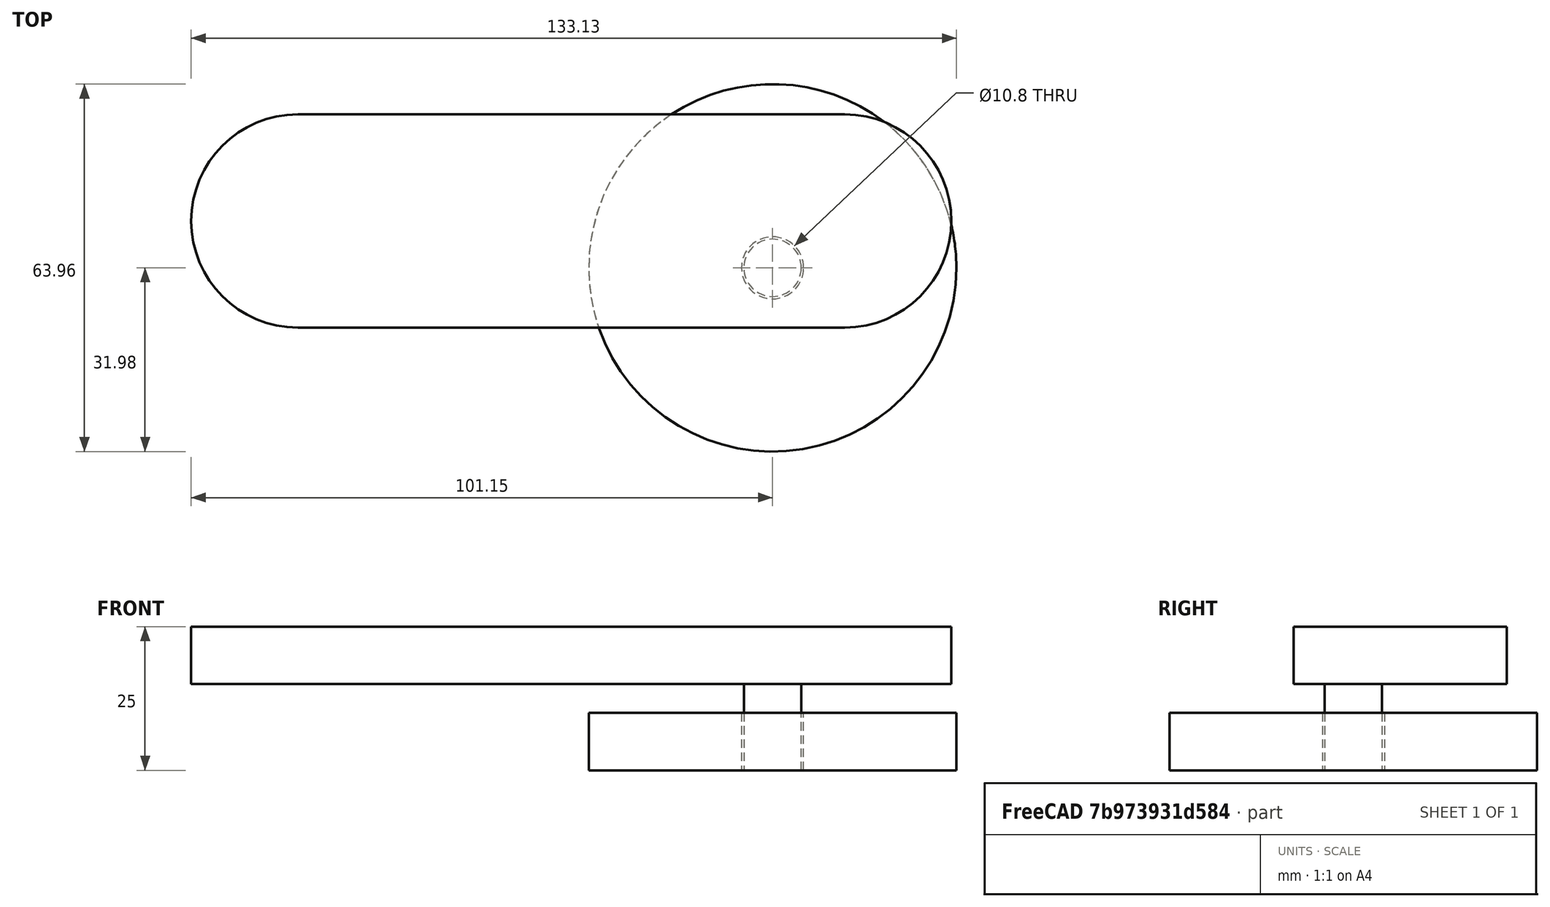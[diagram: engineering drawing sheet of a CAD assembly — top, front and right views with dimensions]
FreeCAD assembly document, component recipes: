
FREECAD ASSEMBLY — COMPONENT RECIPES ("assembly")

This assembly document has 3 components, labeled P0..P2 below (a component is one placed body or linked part). 3 of them carry a construction recipe — the FreeCAD feature program that regenerates the part from scratch, quoted from this document or its linked companion documents; the rest are supplied as boundary geometry only. No exploded tour is included for this assembly.
COMPONENT P0 — recipe-attached ("Cuerpo003", modeled in this document).
Construction recipe (the document's own serialized feature program — sketch geometry with constraints, then the solid features built on it; lengths are millimeters unless a unit is written):

FEATURE [Sketcher::SketchObject] Sketch
  ArcFitTolerance = 1e-06
  AttachmentSupport = -> [XY_Plane]
  FullyConstrained = false
  MakeInternals = false
  MapMode = 5
  sketch-geometry (2):
    g0: Circle CenterX=0 CenterY=0 CenterZ=0 NormalX=0 NormalY=0 NormalZ=1 AngleXU=0 Radius=31.9841
    g1: Circle CenterX=0 CenterY=0 CenterZ=0 NormalX=0 NormalY=0 NormalZ=1 AngleXU=0 Radius=5.40099
  constraints (2):
    c: Coincident(g0,g-1)
    c: Coincident(g1,g0)
FEATURE [PartDesign::Pad] Pad
  Direction = (0,0,1)
  Length = 10
  Length2 = 10
  Profile = -> Sketch
  ReferenceAxis = -> Sketch [N_Axis]
  Refine = true
  Suppressed = false
  Type = 0
FEATURE [PartDesign::Body] Body  label="Cuerpo"
  AllowCompound = false
  Group = -> [Sketch,Pad]
  Origin = -> Origin
  Tip = -> Pad
COMPONENT P1 — recipe-attached ("Cuerpo004", modeled in this document).
Construction recipe (the document's own serialized feature program — sketch geometry with constraints, then the solid features built on it; lengths are millimeters unless a unit is written):

FEATURE [Sketcher::SketchObject] Sketch001
  ArcFitTolerance = 1e-06
  AttachmentSupport = -> [XY_Plane001]
  FullyConstrained = true
  MakeInternals = false
  MapMode = 5
  sketch-geometry (1):
    g0: Circle CenterX=0 CenterY=0 CenterZ=0 NormalX=0 NormalY=0 NormalZ=1 AngleXU=0 Radius=5
  constraints (2):
    c: Diameter(g0) = 10
    c: Coincident(g0,g-1)
FEATURE [PartDesign::Pad] Pad001
  Direction = (0,0,1)
  Length = 15
  Length2 = 10
  Profile = -> Sketch001
  ReferenceAxis = -> Sketch001 [N_Axis]
  Refine = true
  Suppressed = false
  Type = 0
FEATURE [PartDesign::Body] Body001  label="Cuerpo001"
  AllowCompound = false
  Group = -> [Sketch001,Pad001]
  Origin = -> Origin001
  Tip = -> Pad001
COMPONENT P2 — recipe-attached ("Cuerpo005", modeled in this document).
Construction recipe (the document's own serialized feature program — sketch geometry with constraints, then the solid features built on it; lengths are millimeters unless a unit is written):

FEATURE [Sketcher::SketchObject] Sketch002
  ArcFitTolerance = 1e-06
  AttachmentSupport = -> [XY_Plane002]
  FullyConstrained = false
  MakeInternals = false
  MapMode = 5
  sketch-geometry (4):
    g0: ArcOfCircle CenterX=12.5522 CenterY=8.15709 CenterZ=0 NormalX=0 NormalY=0 NormalZ=1 AngleXU=0 Radius=18.555 StartAngle=4.71239 EndAngle=7.85398
    g1: ArcOfCircle CenterX=-82.5935 CenterY=8.15709 CenterZ=0 NormalX=0 NormalY=0 NormalZ=1 AngleXU=0 Radius=18.555 StartAngle=1.5708 EndAngle=4.71239
    g2: LineSegment StartX=12.5522 StartY=-10.398 StartZ=0 EndX=-82.5935 EndY=-10.398 EndZ=0
    g3: LineSegment StartX=12.5522 StartY=26.7121 StartZ=0 EndX=-82.5935 EndY=26.7121 EndZ=0
  constraints (6):
    c: Tangent(g0,g2) = 1.5708
    c: Tangent(g0,g3) = -1.5708
    c: Tangent(g1,g2) = 1.5708
    c: Tangent(g1,g3) = -1.5708
    c: Equal(g0,g1)
    c: Horizontal(g2)
FEATURE [PartDesign::Pad] Pad002
  Direction = (0,0,1)
  Length = 10
  Length2 = 10
  Profile = -> Sketch002
  ReferenceAxis = -> Sketch002 [N_Axis]
  Refine = true
  Suppressed = false
  Type = 0
FEATURE [PartDesign::Body] Body002  label="Cuerpo002"
  AllowCompound = false
  Group = -> [Sketch002,Pad002]
  Origin = -> Origin002
  Placement = pos=(0,0,15) rot=(0,0,1;0rad)
  Tip = -> Pad002
PROVENANCE & LICENSES
A FreeCAD (.FCStd) document from a public repository crawl; recipes are the document's own serialized feature recipes (and, for linked parts, companion documents' recipes).
License: as declared in the source repository (recorded in the dataset sidecar).
